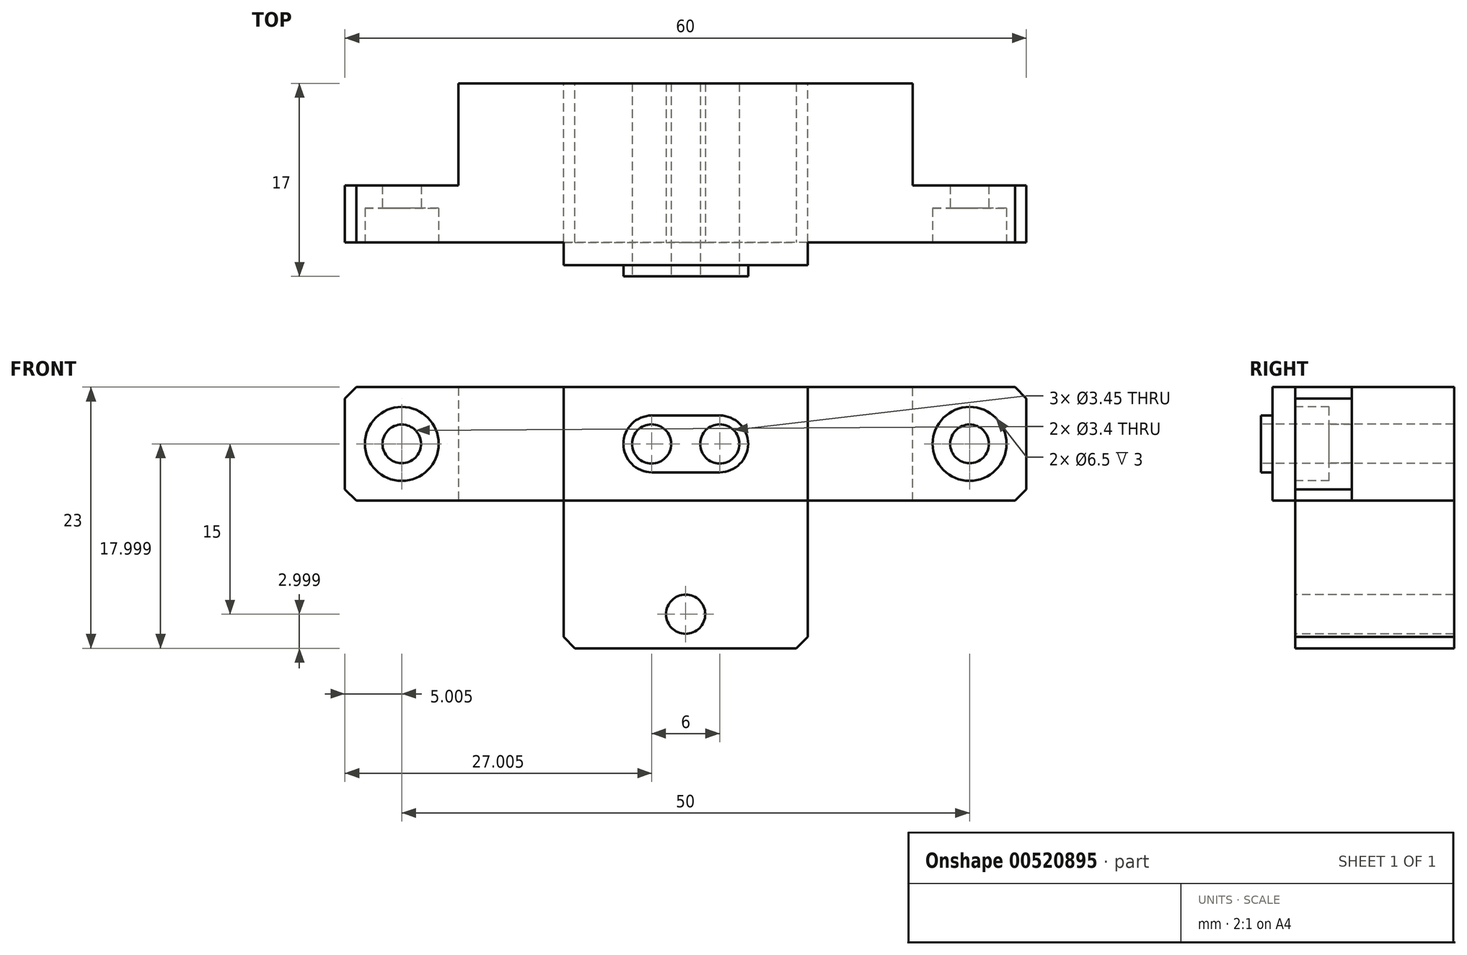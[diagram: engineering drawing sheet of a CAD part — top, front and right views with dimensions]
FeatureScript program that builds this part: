
annotation { "Feature Type Name" : "Feature", "Feature Type Description" : "" }
export const myFeature = defineFeature(function(context is Context, id is Id, definition is map)
    precondition{}
    {
        {
            var Q0;
            Q0=qCreatedBy(makeId("Front.planeOp"),FACE);
            var sketch = newSketch(context, id + "F0", { "sketchPlane" : qUnion([Q0])});
            skLineSegment(sketch, "E0.bottom", {"start": v(-26.09, 6.52) * mm, "end": v(33.91, 6.52) * mm});
            skLineSegment(sketch, "E0.top", {"start": v(-6.84, -16.48) * mm, "end": v(14.66, -16.48) * mm});
            skLineSegment(sketch, "E0.left", {"start": v(-26.09, 6.52) * mm, "end": v(-26.09, -3.48) * mm});
            skLineSegment(sketch, "E0.right", {"start": v(33.91, 6.52) * mm, "end": v(33.91, -3.48) * mm});
            skLineSegment(sketch, "E1", {"start": v(-6.84, -16.48) * mm, "end": v(-6.84, -3.48) * mm});
            skLineSegment(sketch, "E2", {"start": v(-6.84, -3.48) * mm, "end": v(-26.09, -3.48) * mm});
            skLineSegment(sketch, "E3", {"start": v(14.66, -16.48) * mm, "end": v(14.66, -3.48) * mm});
            skLineSegment(sketch, "E4", {"start": v(14.66, -3.48) * mm, "end": v(33.91, -3.48) * mm});
            skSolve(sketch);
        }
        {
            var Q0;
            Q0=makeQuery(id+"F0.imprint","IMPRINT",FACE,{"disambiguationData":[TD([[makeQuery(id+"F0.imprint","IMPRINT",EDGE,{"derivedFrom":sQuery(id+"F0.wireOp",EDGE,"E0.bottom")}),-1.0]])]});
            extrude(context, id + "F1", {"entities" : qUnion([Q0]), "depth" : 16 * mm, "offsetDistance" : 25 * mm});
        }
        {
            var Q0;
            Q0=makeQuery(id+"F1.opExtrude","CAP_FACE",FACE,{"disambiguationData":[OSD([sQuery(id+"F0.wireOp",EDGE,"E0.bottom"),sQuery(id+"F0.wireOp",EDGE,"E0.top"),sQuery(id+"F0.wireOp",EDGE,"E0.left"),sQuery(id+"F0.wireOp",EDGE,"E0.right"),sQuery(id+"F0.wireOp",EDGE,"E1"),sQuery(id+"F0.wireOp",EDGE,"E2"),sQuery(id+"F0.wireOp",EDGE,"E3"),sQuery(id+"F0.wireOp",EDGE,"E4")])],"isStart":false});
            var sketch = newSketch(context, id + "F2", { "sketchPlane" : qUnion([Q0])});
            skLineSegment(sketch, "E5", {"start": v(-6.84, -3.48) * mm, "end": v(-6.84, 6.52) * mm});
            skLineSegment(sketch, "E6", {"start": v(-6.84, 6.52) * mm, "end": v(-26.09, 6.52) * mm});
            skLineSegment(sketch, "E7", {"start": v(-26.09, 6.52) * mm, "end": v(-26.09, -3.48) * mm});
            skLineSegment(sketch, "E8", {"start": v(-26.09, -3.48) * mm, "end": v(-6.84, -3.48) * mm});
            skLineSegment(sketch, "E9", {"start": v(14.66, -3.48) * mm, "end": v(-6.84, -3.48) * mm});
            skLineSegment(sketch, "E10", {"start": v(-6.84, -3.48) * mm, "end": v(-6.84, -16.48) * mm});
            skLineSegment(sketch, "E11", {"start": v(-6.84, -16.48) * mm, "end": v(14.66, -16.48) * mm});
            skLineSegment(sketch, "E12", {"start": v(14.66, -16.48) * mm, "end": v(14.66, -3.48) * mm});
            skLineSegment(sketch, "E13", {"start": v(14.66, -3.48) * mm, "end": v(14.66, 6.52) * mm});
            skLineSegment(sketch, "E14", {"start": v(14.66, 6.52) * mm, "end": v(33.91, 6.52) * mm});
            skLineSegment(sketch, "E15", {"start": v(33.91, 6.52) * mm, "end": v(33.91, -3.48) * mm});
            skLineSegment(sketch, "E16", {"start": v(33.91, -3.48) * mm, "end": v(14.66, -3.48) * mm});
            skSolve(sketch);
        }
        {
            var Q0;
            Q0=makeQuery(id+"F2.imprint","IMPRINT",FACE,{"disambiguationData":[TD([[makeQuery(id+"F2.imprint","IMPRINT",EDGE,{"derivedFrom":sQuery(id+"F2.wireOp",EDGE,"E9")}),1.0]])]});
            var Q1;
            Q1=makeQuery(id+"F2.imprint","IMPRINT",FACE,{"disambiguationData":[TD([[makeQuery(id+"F2.imprint","IMPRINT",EDGE,{"derivedFrom":sQuery(id+"F2.wireOp",EDGE,"E5")}),1.0]])]});
            var Q2;
            Q2=makeQuery(id+"F2.imprint","IMPRINT",FACE,{"disambiguationData":[TD([[makeQuery(id+"F2.imprint","IMPRINT",EDGE,{"derivedFrom":sQuery(id+"F2.wireOp",EDGE,"E13")}),-1.0]])]});
            extrude(context, id + "F3", {"entities" : qUnion([Q0, Q1, Q2]), "operationType" : NewBodyOperationType.REMOVE, "oppositeDirection" : true, "depth" : 2 * mm, "offsetDistance" : 25 * mm});
        }
        {
            var Q0;
            Q0=makeQuery(id+"F3.boolean.opBoolean","COPY",FACE,{"derivedFrom":makeQuery(id+"F3.opExtrude","CAP_FACE",FACE,{"disambiguationData":[OSD([sQuery(id+"F2.wireOp",EDGE,"E5"),sQuery(id+"F2.wireOp",EDGE,"E6"),sQuery(id+"F2.wireOp",EDGE,"E7"),sQuery(id+"F2.wireOp",EDGE,"E8")])],"isStart":false})});
            var sketch = newSketch(context, id + "F4", { "sketchPlane" : qUnion([Q0])});
            skCircle(sketch, "E17", {"center": v(-21.09, 1.52) * mm, "radius": 3.25 * mm});
            skPoint(sketch, "E17.centerSnap0", {"position": v(-26.09, 1.52) * mm});
            skCircle(sketch, "E18", {"center": v(28.91, 1.52) * mm, "radius": 3.25 * mm});
            skSolve(sketch);
        }
        {
            var Q0;
            Q0 = qSketchRegion(id + "F4", true);
            extrude(context, id + "F5", {"entities" : qUnion([Q0]), "operationType" : NewBodyOperationType.REMOVE, "oppositeDirection" : true, "depth" : 3 * mm, "offsetDistance" : 25 * mm});
        }
        {
            var Q0;
            Q0=makeQuery(id+"F5.boolean.opBoolean","COPY",FACE,{"derivedFrom":makeQuery(id+"F5.opExtrude","CAP_FACE",FACE,{"disambiguationData":[OSD([sQuery(id+"F4.wireOp",EDGE,"E17")])],"isStart":false})});
            var sketch = newSketch(context, id + "F6", { "sketchPlane" : qUnion([Q0])});
            skCircle(sketch, "E19", {"center": v(-21.09, 1.52) * mm, "radius": 1.7 * mm});
            skSolve(sketch);
        }
        {
            var Q0;
            Q0=makeQuery(id+"F5.boolean.opBoolean","COPY",FACE,{"derivedFrom":makeQuery(id+"F5.opExtrude","CAP_FACE",FACE,{"disambiguationData":[OSD([sQuery(id+"F4.wireOp",EDGE,"E18")])],"isStart":false})});
            var sketch = newSketch(context, id + "F7", { "sketchPlane" : qUnion([Q0])});
            skCircle(sketch, "E20", {"center": v(28.91, 1.52) * mm, "radius": 1.7 * mm});
            skSolve(sketch);
        }
        {
            var Q0;
            Q0=makeQuery(id+"F6.imprint","IMPRINT",FACE,{"disambiguationData":[TD([[makeQuery(id+"F6.imprint","IMPRINT",EDGE,{"derivedFrom":sQuery(id+"F6.wireOp",EDGE,"E19")}),1.0]])]});
            var Q1;
            Q1=makeQuery(id+"F7.imprint","IMPRINT",FACE,{"disambiguationData":[TD([[makeQuery(id+"F7.imprint","IMPRINT",EDGE,{"derivedFrom":sQuery(id+"F7.wireOp",EDGE,"E20")}),1.0]])]});
            extrude(context, id + "F8", {"entities" : qUnion([Q0, Q1]), "operationType" : NewBodyOperationType.REMOVE, "oppositeDirection" : true, "depth" : 25 * mm, "offsetDistance" : 25 * mm});
        }
        {
            var Q0;
            Q0=makeQuery(id+"F1.opExtrude","CAP_FACE",FACE,{"disambiguationData":[OSD([sQuery(id+"F0.wireOp",EDGE,"E0.bottom"),sQuery(id+"F0.wireOp",EDGE,"E0.top"),sQuery(id+"F0.wireOp",EDGE,"E0.left"),sQuery(id+"F0.wireOp",EDGE,"E0.right"),sQuery(id+"F0.wireOp",EDGE,"E1"),sQuery(id+"F0.wireOp",EDGE,"E2"),sQuery(id+"F0.wireOp",EDGE,"E3"),sQuery(id+"F0.wireOp",EDGE,"E4")])],"isStart":true});
            var sketch = newSketch(context, id + "F9", { "sketchPlane" : qUnion([Q0])});
            skLineSegment(sketch, "E21", {"start": v(-23.91, -3.48) * mm, "end": v(-23.91, 6.52) * mm});
            skLineSegment(sketch, "E22", {"start": v(-23.91, 6.52) * mm, "end": v(-33.91, 6.52) * mm});
            skLineSegment(sketch, "E23", {"start": v(-33.91, 6.52) * mm, "end": v(-33.91, -3.48) * mm});
            skLineSegment(sketch, "E24", {"start": v(-33.91, -3.48) * mm, "end": v(-23.91, -3.48) * mm});
            skLineSegment(sketch, "E25", {"start": v(16.09, 6.52) * mm, "end": v(16.09, -3.48) * mm});
            skLineSegment(sketch, "E26", {"start": v(16.09, -3.48) * mm, "end": v(26.09, -3.48) * mm});
            skLineSegment(sketch, "E27", {"start": v(26.09, -3.48) * mm, "end": v(26.09, 6.52) * mm});
            skLineSegment(sketch, "E28", {"start": v(26.09, 6.52) * mm, "end": v(16.09, 6.52) * mm});
            skSolve(sketch);
        }
        {
            var Q0;
            Q0=makeQuery(id+"F9.imprint","IMPRINT",FACE,{"disambiguationData":[TD([[makeQuery(id+"F9.imprint","IMPRINT",EDGE,{"derivedFrom":sQuery(id+"F9.wireOp",EDGE,"E25")}),1.0]])]});
            var Q1;
            Q1=makeQuery(id+"F9.imprint","IMPRINT",FACE,{"disambiguationData":[TD([[makeQuery(id+"F9.imprint","IMPRINT",EDGE,{"derivedFrom":sQuery(id+"F9.wireOp",EDGE,"E21")}),1.0]])]});
            extrude(context, id + "F10", {"entities" : qUnion([Q0, Q1]), "operationType" : NewBodyOperationType.REMOVE, "oppositeDirection" : true, "depth" : 9 * mm, "offsetDistance" : 25 * mm});
        }
        {
            var Q0;
            Q0=makeQuery(id+"F3.boolean.opBoolean","COPY",FACE,{"derivedFrom":makeQuery(id+"F3.opExtrude","CAP_FACE",FACE,{"disambiguationData":[OSD([sQuery(id+"F2.wireOp",EDGE,"E13"),sQuery(id+"F2.wireOp",EDGE,"E14"),sQuery(id+"F2.wireOp",EDGE,"E15"),sQuery(id+"F2.wireOp",EDGE,"E16")])],"isStart":false})});
            var sketch = newSketch(context, id + "F11", { "sketchPlane" : qUnion([Q0])});
            skCircle(sketch, "E29", {"center": v(0.91, 1.52) * mm, "radius": 1.73 * mm});
            skPoint(sketch, "E29.centerSnap0", {"position": v(14.66, 1.52) * mm});
            skCircle(sketch, "E30", {"center": v(6.91, 1.52) * mm, "radius": 1.73 * mm});
            skSolve(sketch);
        }
        {
            var Q0;
            Q0=qCreatedBy(makeId("Front.planeOp"),FACE);
            var sketch = newSketch(context, id + "F12", { "sketchPlane" : qUnion([Q0])});
            skArc(sketch, "E31", {"start": v(6.91, -0.98) * mm, "mid": v(9.41, 1.52) * mm, "end": v(6.91, 4.02) * mm});
            skArc(sketch, "E32", {"start": v(0.93, 4.02) * mm, "mid": v(-1.57, 1.52) * mm, "end": v(0.93, -0.98) * mm});
            skLineSegment(sketch, "E33", {"start": v(0.93, 4.02) * mm, "end": v(6.91, 4.02) * mm});
            skLineSegment(sketch, "E34", {"start": v(6.91, -0.98) * mm, "end": v(0.93, -0.98) * mm});
            skSolve(sketch);
        }
        {
            var Q0;
            Q0=makeQuery(id+"F12.imprint","IMPRINT",FACE,{"disambiguationData":[TD([[makeQuery(id+"F12.imprint","IMPRINT",EDGE,{"derivedFrom":sQuery(id+"F12.wireOp",EDGE,"E31")}),1.0]])]});
            extrude(context, id + "F13", {"entities" : qUnion([Q0]), "operationType" : NewBodyOperationType.ADD, "depth" : 17 * mm, "offsetDistance" : 25 * mm});
        }
        {
            var Q0;
            Q0 = qSketchRegion(id + "F11", true);
            extrude(context, id + "F14", {"entities" : qUnion([Q0]), "operationType" : NewBodyOperationType.REMOVE, "endBound" : BoundingType.SYMMETRIC, "oppositeDirection" : true, "depth" : 30 * mm, "offsetDistance" : 25 * mm});
        }
        {
            var Q0;
            Q0=makeQuery(id+"F3.boolean.opBoolean","COPY",FACE,{"derivedFrom":makeQuery(id+"F3.opExtrude","CAP_FACE",FACE,{"disambiguationData":[OSD([sQuery(id+"F2.wireOp",EDGE,"E9"),sQuery(id+"F2.wireOp",EDGE,"E10"),sQuery(id+"F2.wireOp",EDGE,"E11"),sQuery(id+"F2.wireOp",EDGE,"E12")])],"isStart":false})});
            var sketch = newSketch(context, id + "F15", { "sketchPlane" : qUnion([Q0])});
            skCircle(sketch, "E35", {"center": v(3.91, -13.48) * mm, "radius": 1.73 * mm});
            skPoint(sketch, "E35.centerSnap0", {"position": v(3.91, -16.48) * mm});
            skSolve(sketch);
        }
        {
            var Q0;
            Q0=makeQuery(id+"F15.imprint","IMPRINT",FACE,{"disambiguationData":[TD([[makeQuery(id+"F15.imprint","IMPRINT",EDGE,{"derivedFrom":sQuery(id+"F15.wireOp",EDGE,"E35")}),1.0]])]});
            extrude(context, id + "F16", {"entities" : qUnion([Q0]), "operationType" : NewBodyOperationType.REMOVE, "oppositeDirection" : true, "depth" : 25 * mm, "offsetDistance" : 25 * mm});
        }
        {
            var Q0;
            Q0=makeQuery(id+"F1.opExtrude","SWEPT_EDGE",EDGE,{"disambiguationData":[OSD([sQuery(id+"F0.wireOp",EDGE,"E0.top"),sQuery(id+"F0.wireOp",EDGE,"E1")])]});
            var Q1;
            Q1=makeQuery(id+"F1.opExtrude","SWEPT_EDGE",EDGE,{"disambiguationData":[OSD([sQuery(id+"F0.wireOp",EDGE,"E0.top"),sQuery(id+"F0.wireOp",EDGE,"E3")])]});
            var Q2;
            Q2=makeQuery(id+"F1.opExtrude","SWEPT_EDGE",EDGE,{"disambiguationData":[OSD([sQuery(id+"F0.wireOp",EDGE,"E0.right"),sQuery(id+"F0.wireOp",EDGE,"E4")])]});
            var Q3;
            Q3=makeQuery(id+"F1.opExtrude","SWEPT_EDGE",EDGE,{"disambiguationData":[OSD([sQuery(id+"F0.wireOp",EDGE,"E0.bottom"),sQuery(id+"F0.wireOp",EDGE,"E0.right")])]});
            var Q4;
            Q4=makeQuery(id+"F1.opExtrude","SWEPT_EDGE",EDGE,{"disambiguationData":[OSD([sQuery(id+"F0.wireOp",EDGE,"E0.bottom"),sQuery(id+"F0.wireOp",EDGE,"E0.left")])]});
            var Q5;
            Q5=makeQuery(id+"F1.opExtrude","SWEPT_EDGE",EDGE,{"disambiguationData":[OSD([sQuery(id+"F0.wireOp",EDGE,"E0.left"),sQuery(id+"F0.wireOp",EDGE,"E2")])]});
            var Q6;
            Q6=makeQuery(id+"F10.boolean.opBoolean","COPY",EDGE,{"derivedFrom":makeQuery(id+"F10.opExtrude","SWEPT_EDGE",EDGE,{"disambiguationData":[OSD([sQuery(id+"F0.wireOp",EDGE,"E2"),sQuery(id+"F9.wireOp",EDGE,"E25"),sQuery(id+"F9.wireOp",EDGE,"E26")])]})});
            var Q7;
            Q7=makeQuery(id+"F10.boolean.opBoolean","COPY",EDGE,{"derivedFrom":makeQuery(id+"F10.opExtrude","SWEPT_EDGE",EDGE,{"disambiguationData":[OSD([sQuery(id+"F0.wireOp",EDGE,"E0.bottom"),sQuery(id+"F9.wireOp",EDGE,"E25"),sQuery(id+"F9.wireOp",EDGE,"E28")])]})});
            var Q8;
            Q8=makeQuery(id+"F10.boolean.opBoolean","COPY",EDGE,{"derivedFrom":makeQuery(id+"F10.opExtrude","SWEPT_EDGE",EDGE,{"disambiguationData":[OSD([sQuery(id+"F0.wireOp",EDGE,"E0.bottom"),sQuery(id+"F9.wireOp",EDGE,"E21"),sQuery(id+"F9.wireOp",EDGE,"E22")])]})});
            var Q9;
            Q9=makeQuery(id+"F10.boolean.opBoolean","COPY",EDGE,{"derivedFrom":makeQuery(id+"F10.opExtrude","SWEPT_EDGE",EDGE,{"disambiguationData":[OSD([sQuery(id+"F0.wireOp",EDGE,"E4"),sQuery(id+"F9.wireOp",EDGE,"E21"),sQuery(id+"F9.wireOp",EDGE,"E24")])]})});
            chamfer(context, id + "F17", {"entities" : qUnion([Q0, Q1, Q2, Q3, Q4, Q5, Q6, Q7, Q8, Q9]), "width" : 1 * mm, "tangentPropagation" : true});
        }
    });
